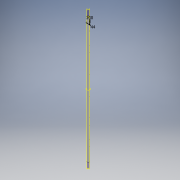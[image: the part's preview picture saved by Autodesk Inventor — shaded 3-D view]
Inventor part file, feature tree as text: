
AUTODESK INVENTOR PART (.ipt)
format: ipt  version: 2017 (Build 210142000, 142)  size: 161,792 bytes
history: native  units: mm
features: extrude x2, sketch x2, pattern_linear x1, projected_geometry x1
ambient origin geometry x8: Origin, YZ Plane, XZ Plane, XY Plane, X Axis, Y Axis, Z Axis, Center Point
bodies: Solid1 (feature_tree)
feature tree (6):
  extrude  "Extrusion1"  Depth=72.0mm
  extrude  "Extrusion2"  Depth=44.0mm
  pattern_linear  "Rectangular Pattern1"  Count1=400 Spacing1=0.0mm
  sketch  "Sketch1"  dims[d0=76.0mm d1=72.0mm]
  sketch  "Sketch2"  dims[d2=2000.0mm d3=0.0mm d4=44.0mm d6=4000.0mm d7=0.0mm d8=190.0mm d10=200.0mm d11=2000.0mm d12=0.0mm d18=200.0mm]
  projected_geometry  "Projected Loop1"
